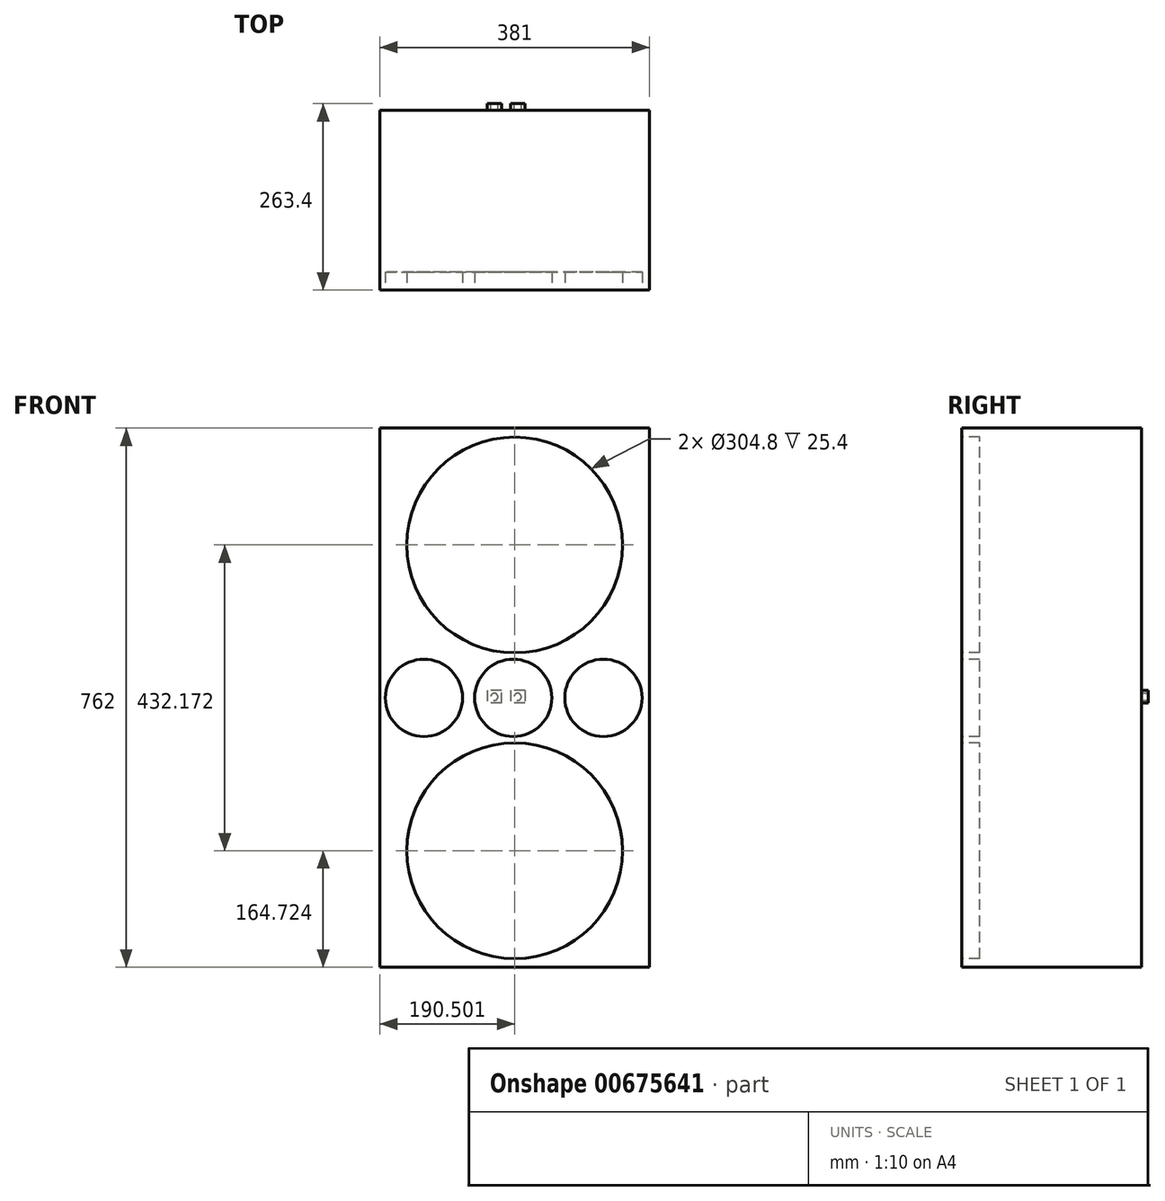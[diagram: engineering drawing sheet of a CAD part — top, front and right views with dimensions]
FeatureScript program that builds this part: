
annotation { "Feature Type Name" : "Feature", "Feature Type Description" : "" }
export const myFeature = defineFeature(function(context is Context, id is Id, definition is map)
    precondition{}
    {
        {
            var Q0;
            Q0=qCreatedBy(makeId("Front.planeOp"),FACE);
            var sketch = newSketch(context, id + "F0", { "sketchPlane" : qUnion([Q0])});
            skLineSegment(sketch, "E0.bottom", {"start": v(-171.9, 381.19) * mm, "end": v(209.1, 381.19) * mm});
            skLineSegment(sketch, "E0.top", {"start": v(-171.9, -380.81) * mm, "end": v(209.1, -380.81) * mm});
            skLineSegment(sketch, "E0.left", {"start": v(-171.9, 381.19) * mm, "end": v(-171.9, -380.81) * mm});
            skLineSegment(sketch, "E0.right", {"start": v(209.1, 381.19) * mm, "end": v(209.1, -380.81) * mm});
            skSolve(sketch);
        }
        {
            var Q0;
            Q0 = qSketchRegion(id + "F0", true);
            extrude(context, id + "F1", {"entities" : qUnion([Q0]), "depth" : 254 * mm, "offsetDistance" : 25.4 * mm});
        }
        {
            var Q0;
            Q0=makeQuery(id+"F1.opExtrude","CAP_FACE",FACE,{"disambiguationData":[OSD([sQuery(id+"F0.wireOp",EDGE,"E0.bottom"),sQuery(id+"F0.wireOp",EDGE,"E0.top"),sQuery(id+"F0.wireOp",EDGE,"E0.left"),sQuery(id+"F0.wireOp",EDGE,"E0.right")])],"isStart":false});
            var sketch = newSketch(context, id + "F2", { "sketchPlane" : qUnion([Q0])});
            skCircle(sketch, "E1", {"center": v(18.6, 216.09) * mm, "radius": 152.4 * mm});
            skLineSegment(sketch, "E2", {"start": v(-171.9, 0) * mm, "end": v(209.1, 0) * mm});
            skCircle(sketch, "E3.MirrorC", {"center": v(18.6, -216.09) * mm, "radius": 152.4 * mm});
            skSolve(sketch);
        }
        {
            var Q0;
            Q0 = qSketchRegion(id + "F2", true);
            extrude(context, id + "F3", {"entities" : qUnion([Q0]), "operationType" : NewBodyOperationType.REMOVE, "oppositeDirection" : true, "depth" : 25.4 * mm, "offsetDistance" : 25.4 * mm});
        }
        {
            var Q0;
            Q0=makeQuery(id+"F1.opExtrude","CAP_FACE",FACE,{"disambiguationData":[OSD([sQuery(id+"F0.wireOp",EDGE,"E0.bottom"),sQuery(id+"F0.wireOp",EDGE,"E0.top"),sQuery(id+"F0.wireOp",EDGE,"E0.left"),sQuery(id+"F0.wireOp",EDGE,"E0.right")])],"isStart":false});
            var sketch = newSketch(context, id + "F4", { "sketchPlane" : qUnion([Q0])});
            skCircle(sketch, "E4", {"center": v(-109.67, 0) * mm, "radius": 54.61 * mm});
            skCircle(sketch, "E5", {"center": v(16.57, 0) * mm, "radius": 54.61 * mm});
            skCircle(sketch, "E6", {"center": v(144.08, 0) * mm, "radius": 54.61 * mm});
            skSolve(sketch);
        }
        {
            var Q0;
            Q0 = qSketchRegion(id + "F4", true);
            extrude(context, id + "F5", {"entities" : qUnion([Q0]), "operationType" : NewBodyOperationType.REMOVE, "oppositeDirection" : true, "depth" : 25.4 * mm, "offsetDistance" : 25.4 * mm});
        }
        {
            var Q0;
            Q0=makeQuery(id+"F1.opExtrude","CAP_FACE",FACE,{"disambiguationData":[OSD([sQuery(id+"F0.wireOp",EDGE,"E0.bottom"),sQuery(id+"F0.wireOp",EDGE,"E0.top"),sQuery(id+"F0.wireOp",EDGE,"E0.left"),sQuery(id+"F0.wireOp",EDGE,"E0.right")])],"isStart":true});
            var sketch = newSketch(context, id + "F6", { "sketchPlane" : qUnion([Q0])});
            skLineSegment(sketch, "E7.bottom", {"start": v(-33.02, 10.29) * mm, "end": v(-12.7, 10.29) * mm});
            skLineSegment(sketch, "E7.top", {"start": v(-33.02, -7.5) * mm, "end": v(-12.7, -7.5) * mm});
            skLineSegment(sketch, "E7.left", {"start": v(-33.02, 10.29) * mm, "end": v(-33.02, -7.5) * mm});
            skLineSegment(sketch, "E7.right", {"start": v(-12.7, 10.29) * mm, "end": v(-12.7, -7.5) * mm});
            skLineSegment(sketch, "E8.bottom", {"start": v(0, 10.29) * mm, "end": v(20.32, 10.29) * mm});
            skLineSegment(sketch, "E8.top", {"start": v(0, -7.5) * mm, "end": v(20.32, -7.5) * mm});
            skLineSegment(sketch, "E9", {"start": v(0, -7.5) * mm, "end": v(0, 10.29) * mm});
            skLineSegment(sketch, "E10", {"start": v(20.32, 10.29) * mm, "end": v(20.32, -7.5) * mm});
            skSolve(sketch);
        }
        {
            var Q0;
            Q0 = qSketchRegion(id + "F6", true);
            extrude(context, id + "F7", {"entities" : qUnion([Q0]), "operationType" : NewBodyOperationType.ADD, "depth" : 9.4 * mm, "offsetDistance" : 25.4 * mm});
        }
        {
            var Q0;
            Q0=makeQuery(id+"F7.opExtrude","CAP_FACE",FACE,{"disambiguationData":[OSD([sQuery(id+"F6.wireOp",EDGE,"E7.bottom"),sQuery(id+"F6.wireOp",EDGE,"E7.top"),sQuery(id+"F6.wireOp",EDGE,"E7.left"),sQuery(id+"F6.wireOp",EDGE,"E7.right")])],"isStart":false});
            var sketch = newSketch(context, id + "F8", { "sketchPlane" : qUnion([Q0])});
            skCircle(sketch, "E11", {"center": v(-22.86, 1.4) * mm, "radius": 5.08 * mm});
            skPoint(sketch, "E11.centerSnap0", {"position": v(-22.86, 10.29) * mm});
            skPoint(sketch, "E11.centerSnap1", {"position": v(-33.02, 1.4) * mm});
            skSolve(sketch);
        }
        {
            var Q0;
            Q0 = qSketchRegion(id + "F8", true);
            extrude(context, id + "F9", {"entities" : qUnion([Q0]), "operationType" : NewBodyOperationType.REMOVE, "oppositeDirection" : true, "depth" : 10.16 * mm, "offsetDistance" : 25.4 * mm});
        }
        {
            var Q0;
            Q0=makeQuery(id+"F7.opExtrude","CAP_FACE",FACE,{"disambiguationData":[OSD([sQuery(id+"F6.wireOp",EDGE,"E8.bottom"),sQuery(id+"F6.wireOp",EDGE,"E8.top"),sQuery(id+"F6.wireOp",EDGE,"E9"),sQuery(id+"F6.wireOp",EDGE,"E10")])],"isStart":false});
            var sketch = newSketch(context, id + "F10", { "sketchPlane" : qUnion([Q0])});
            skCircle(sketch, "E12", {"center": v(10.16, 1.4) * mm, "radius": 5.08 * mm});
            skPoint(sketch, "E12.centerSnap0", {"position": v(10.16, 10.29) * mm});
            skPoint(sketch, "E12.centerSnap1", {"position": v(0, 1.4) * mm});
            skSolve(sketch);
        }
        {
            var Q0;
            Q0 = qSketchRegion(id + "F10", true);
            extrude(context, id + "F11", {"entities" : qUnion([Q0]), "operationType" : NewBodyOperationType.REMOVE, "oppositeDirection" : true, "depth" : 10.16 * mm, "offsetDistance" : 25.4 * mm});
        }
    });
